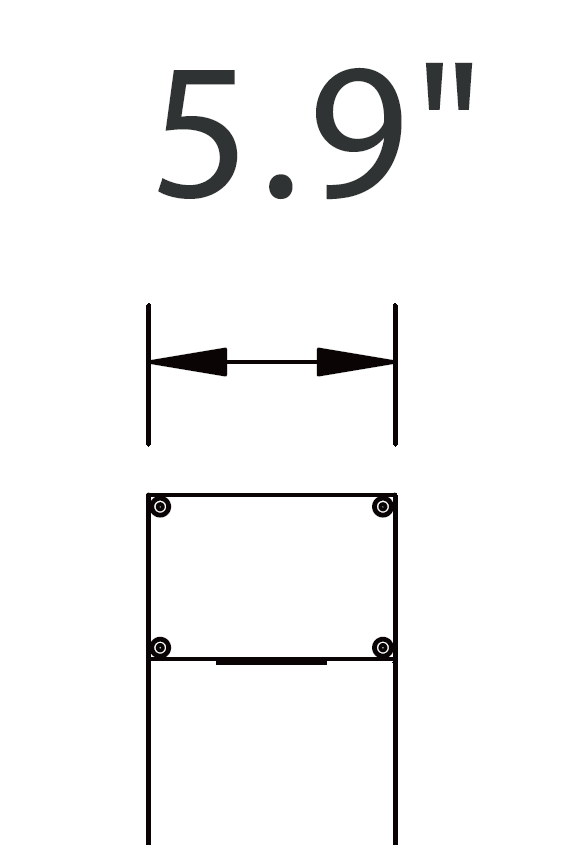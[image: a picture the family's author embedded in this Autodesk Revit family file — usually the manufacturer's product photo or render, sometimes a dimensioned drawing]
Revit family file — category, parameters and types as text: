
# Revit family: Lin1
name_source: partatom
category: Lighting Fixtures
units: mm (PartAtom-declared; Revit-internal decimal feet)

## family parameters
Always vertical = Yes
Cut with Voids When Loaded = No
Light Source = Yes
Maintain Annotation Orientation = No
OmniClass Number = 23.80.70.00
OmniClass Title = Lighting
Part Type = Normal
Room Calculation Point = No
Round Connector Dimension = Use Diameter
Shared = No
Work Plane-Based = No

## types (16) — shared parameters
CRI = 80
Color Filter = 16777215
Default Elevation = 0' - 0"
Dimming Lamp Color Temperature Shift = <None>
H = 9' - 10 3/32"
IP Rating = IP65
Input Voltage = 120-277V
Lamp = LED
Load Classification = Lighting
Manufacturer = Above All Lighting
Power Factor = 0.9
Tilt Angle = 90.00°
URL = https://www.abovealllighting.com

## per-type parameters (varying)
| type | Model | Photometric Web File | Wattage Comments |
| LIN1-30W-3000K-II-9.84ft | LIN1-3030801-II-BK | LIN1-3030801-II-BK.IES | 30W |
| LIN1-30W-3000K-III-9.84ft | LIN1-3030801-III-BK | LIN1-3030801-III-BK.IES | 30W |
| LIN1-30W-3000K-IV-9.84ft | LIN1-3030801-IV-BK | LIN1-3030801-IV-BK.IES | 30W |
| LIN1-30W-3000K-V-9.84ft | LIN1-3030801-V-BK | LIN1-3030801-V-BK.IES | 30W |
| LIN1-40W-3000K-II-9.84ft | LIN1-4030801-II-BK | LIN1-4030801-II-BK.IES | 40W |
| LIN1-40W-3000K-III-9.84ft | LIN1-4030801-III-BK | LIN1-4030801-III-BK.IES | 40W |
| LIN1-40W-3000K-IV-9.84ft | LIN1-4030801-IV-BK | LIN1-4030801-IV-BK.IES | 40W |
| LIN1-40W-3000K-V-9.84ft | LIN1-4030801-V-BK | LIN1-4030801-V-BK.IES | 40W |
| LIN1-50W-3000K-II-9.84ft | LIN1-5030801-II-BK | LIN1-5030801-II-BK.IES | 50W |
| LIN1-50W-3000K-III-9.84ft | LIN1-5030801-III-BK | LIN1-5030801-III-BK.IES | 50W |
| LIN1-50W-3000K-IV-9.84ft | LIN1-5030801-IV-BK | LIN1-6030801-IV-BK.IES | 50W |
| LIN1-50W-3000K-V-9.84ft | LIN1-5030801-V-BK | LIN1-6030801-V-BK.IES | 50W |
| LIN1-60W-3000K-II-9.84ft | LIN1-6030801-II-BK | LIN1-6030801-II-BK.IES | 60W |
| LIN1-60W-3000K-III-9.84ft | LIN1-6030801-III-BK | LIN1-6030801-III-BK.IES | 60W |
| LIN1-60W-3000K-IV-9.84ft | LIN1-6030801-IV-BK | LIN1-6030801-IV-BK.IES | 60W |
| LIN1-60W-3000K-V-9.84ft | LIN1-6030801-V-BK | LIN1-6030801-V-BK.IES | 60W |

## geometry (parser evidence)
native form markers: Sweep x3
no freeform markers — native parametric forms only
